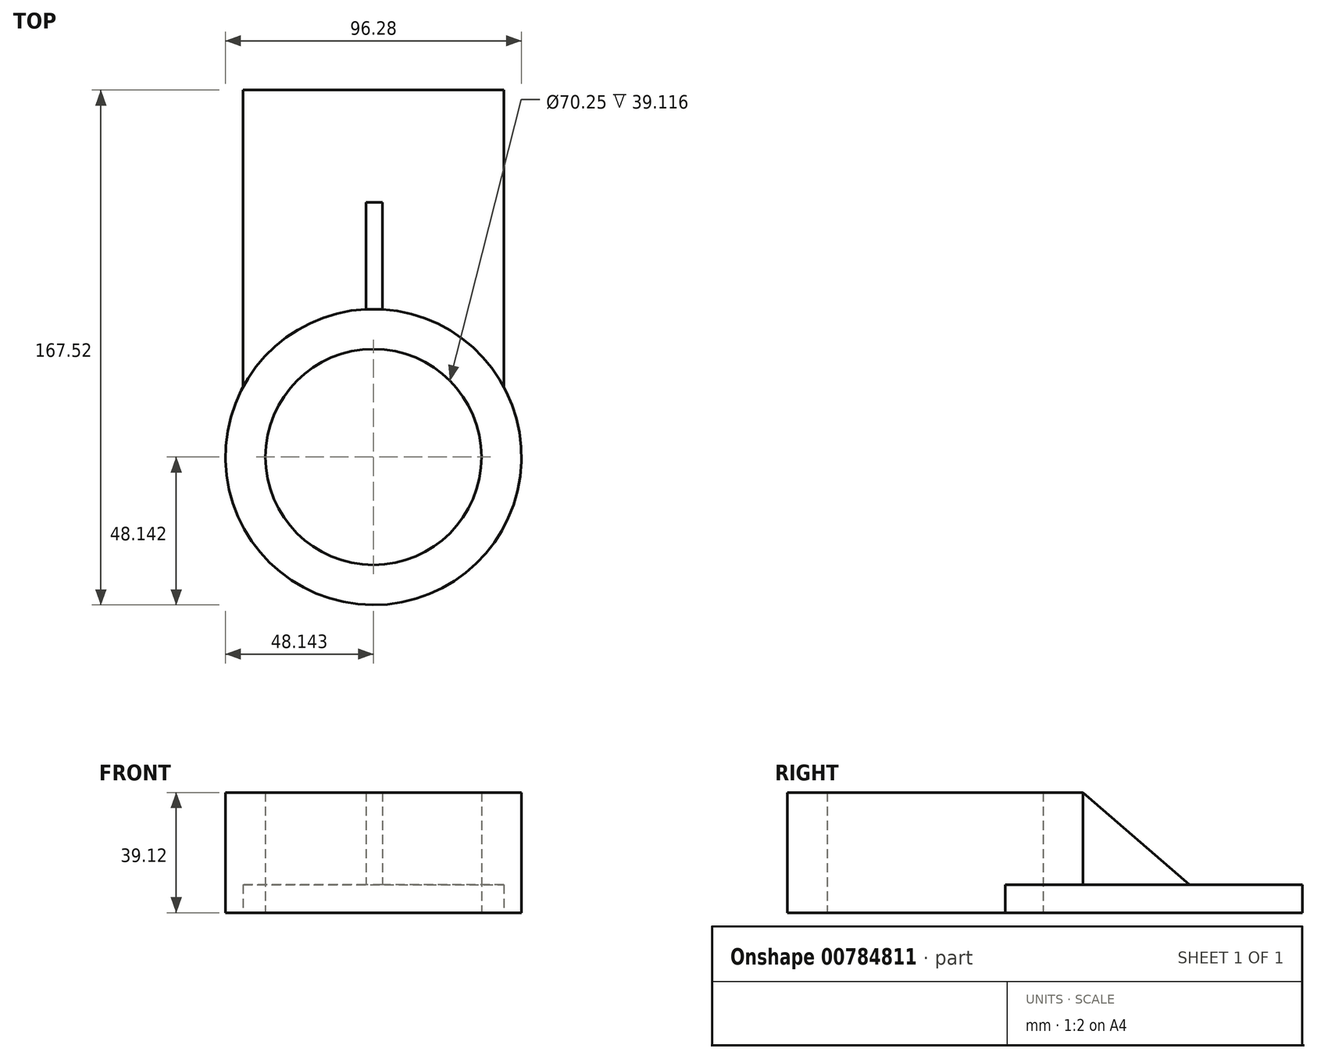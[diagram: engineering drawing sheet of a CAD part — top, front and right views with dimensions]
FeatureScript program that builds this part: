
annotation { "Feature Type Name" : "Feature", "Feature Type Description" : "" }
export const myFeature = defineFeature(function(context is Context, id is Id, definition is map)
    precondition{}
    {
        {
            var Q0;
            Q0=qCreatedBy(makeId("Top.planeOp"),FACE);
            var sketch = newSketch(context, id + "F0", { "sketchPlane" : qUnion([Q0])});
            skLineSegment(sketch, "E0.bottom", {"start": v(-55.5, 70.32) * mm, "end": v(29.3, 70.32) * mm});
            skLineSegment(sketch, "E0.top", {"start": v(-55.5, -9.46) * mm, "end": v(29.3, -9.46) * mm});
            skLineSegment(sketch, "E0.left", {"start": v(-55.5, 70.32) * mm, "end": v(-55.5, -9.46) * mm});
            skLineSegment(sketch, "E0.right", {"start": v(29.3, 70.32) * mm, "end": v(29.3, -9.46) * mm});
            skCircle(sketch, "E1", {"center": v(-13.1, -27.47) * mm, "radius": 48.14 * mm});
            skPoint(sketch, "E1.centerSnap0", {"position": v(-13.1, -9.46) * mm});
            skCircle(sketch, "E2", {"center": v(-13.1, -27.47) * mm, "radius": 35.12 * mm});
            skSolve(sketch);
        }
        {
            var Q0;
            {var subQ1=sQuery(id+"F0.wireOp",EDGE,"E0.top");var subQ5=sQuery(id+"F0.wireOp",EDGE,"E0.left");var subQ6=makeQuery(id+"F0.imprint","INTERSECT",VERTEX,{"derivedFrom":[subQ1,subQ5]});Q0=makeQuery(id+"F0.imprint","IMPRINT",FACE,{"disambiguationData":[TD([[makeQuery(id+"F0.imprint","IMPRINT",EDGE,{"disambiguationData":[TD([[subQ6,-1.0]])],"derivedFrom":subQ1}),1.0]])]});}
            var Q1;
            {var subQ1=sQuery(id+"F0.wireOp",EDGE,"E0.top");var subQ5=sQuery(id+"F0.wireOp",EDGE,"E0.left");var subQ6=makeQuery(id+"F0.imprint","INTERSECT",VERTEX,{"derivedFrom":[subQ1,subQ5]});Q1=makeQuery(id+"F0.imprint","IMPRINT",FACE,{"disambiguationData":[TD([[makeQuery(id+"F0.imprint","IMPRINT",EDGE,{"disambiguationData":[TD([[subQ6,-1.0]])],"derivedFrom":subQ1}),-1.0]])]});}
            extrude(context, id + "F1", {"entities" : qUnion([Q0, Q1]), "depth" : 39.12 * mm, "offsetDistance" : 25.4 * mm});
        }
        {
            var Q0;
            {var subQ0=sQuery(id+"F0.wireOp",EDGE,"E0.bottom");Q0=makeQuery(id+"F0.imprint","IMPRINT",FACE,{"disambiguationData":[TD([[makeQuery(id+"F0.imprint","IMPRINT",EDGE,{"derivedFrom":subQ0}),-1.0]])]});}
            extrude(context, id + "F2", {"entities" : qUnion([Q0]), "operationType" : NewBodyOperationType.ADD, "depth" : 9.14 * mm, "offsetDistance" : 25.4 * mm});
        }
        {
            var Q0;
            Q0=makeQuery(id+"F2.opExtrude","SWEPT_FACE",FACE,{"disambiguationData":[OSD([sQuery(id+"F0.wireOp",EDGE,"E0.bottom")])]});
            extrude(context, id + "F3", {"entities" : qUnion([Q0]), "operationType" : NewBodyOperationType.ADD, "depth" : 21.59 * mm, "offsetDistance" : 25.4 * mm});
        }
        {
            var Q0;
            {var subQ0=sQuery(id+"F0.wireOp",EDGE,"E0.bottom");Q0=makeQuery(id+"F3.boolean.opBoolean","MERGE",FACE,{"derivedFrom":[makeQuery(id+"F2.opExtrude","CAP_FACE",FACE,{"disambiguationData":[OSD([subQ0,sQuery(id+"F0.wireOp",EDGE,"E0.left"),sQuery(id+"F0.wireOp",EDGE,"E0.right"),sQuery(id+"F0.wireOp",EDGE,"E1")])],"isStart":false}),makeQuery(id+"F3.opExtrude","SWEPT_FACE",FACE,{"disambiguationData":[OSD([subQ0]),TDD([makeQuery(id+"F2.opExtrude","CAP_EDGE",EDGE,{"disambiguationData":[OSD([subQ0])],"isStart":false})])]})]});}
            var sketch = newSketch(context, id + "F4", { "sketchPlane" : qUnion([Q0])});
            skPoint(sketch, "E3.startSnap0", {"position": v(-13.1, 91.91) * mm});
            skLineSegment(sketch, "E4.bottom", {"start": v(-10.23, 20.59) * mm, "end": v(-15.52, 20.59) * mm});
            skLineSegment(sketch, "E4.top", {"start": v(-10.23, 55.3) * mm, "end": v(-15.52, 55.3) * mm});
            skLineSegment(sketch, "E4.left", {"start": v(-10.23, 20.59) * mm, "end": v(-10.23, 55.3) * mm});
            skLineSegment(sketch, "E4.right", {"start": v(-15.52, 20.59) * mm, "end": v(-15.52, 55.3) * mm});
            skSolve(sketch);
        }
        {
            var Q0;
            Q0 = qSketchRegion(id + "F4", true);
            extrude(context, id + "F5", {"entities" : qUnion([Q0]), "operationType" : NewBodyOperationType.ADD, "depth" : 29.97 * mm, "offsetDistance" : 25.4 * mm});
        }
        {
            var Q0;
            Q0=makeQuery(id+"F5.opExtrude","SWEPT_FACE",FACE,{"disambiguationData":[OSD([sQuery(id+"F4.wireOp",EDGE,"E4.right")])]});
            var sketch = newSketch(context, id + "F6", { "sketchPlane" : qUnion([Q0])});
            skLineSegment(sketch, "E5", {"start": v(-20.61, 39.12) * mm, "end": v(-55.3, 9.14) * mm});
            skSolve(sketch);
        }
        {
            var Q0;
            Q0=makeQuery(id+"F6.imprint","IMPRINT",FACE,{"disambiguationData":[TD([[makeQuery(id+"F6.imprint","IMPRINT",EDGE,{"derivedFrom":sQuery(id+"F6.wireOp",EDGE,"E5")}),-1.0]])]});
            extrude(context, id + "F7", {"entities" : qUnion([Q0]), "operationType" : NewBodyOperationType.REMOVE, "oppositeDirection" : true, "depth" : 49.78 * mm, "offsetDistance" : 25.4 * mm});
        }
    });
